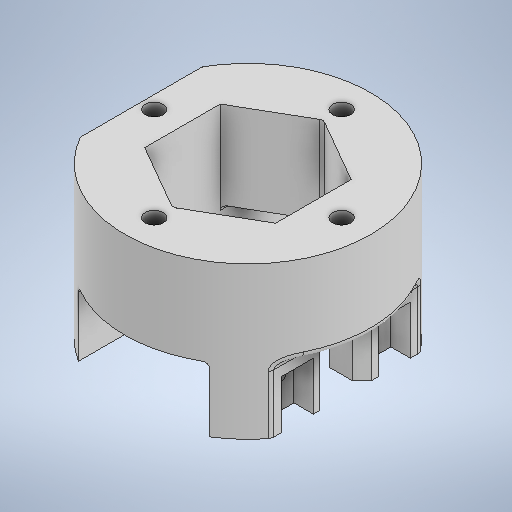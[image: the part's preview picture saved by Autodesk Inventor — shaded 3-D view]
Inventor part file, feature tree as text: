
AUTODESK INVENTOR PART (.ipt)
format: ipt  version: 2025 (Build 290162000, 162)  size: 421,888 bytes
history: native  units: mm
features: sketch x8, extrude x6, hole x2, pattern_circular x2, mirror x2, chamfer x1, fillet x1
ambient origin geometry x8: Origin, YZ Plane, XZ Plane, XY Plane, X Axis, Y Axis, Z Axis, Center Point
bodies: Solid1 (feature_tree)
feature tree (22):
  extrude  "Key Shape"  Depth=36.0mm
  extrude  "Side Walls"  Depth=27.0mm TaperAngle=0.0deg
  hole  "M5 Holes"  [1 undecoded]
  pattern_circular  "Circular Pattern1"  Count=2  [1 undecoded]
  extrude  "M4 Bolt Seats"  Depth=2.0mm
  hole  "M4 Holes"  [1 undecoded]
  mirror  "Mirror1"
  mirror  "Mirror2"
  chamfer  "Chamfer1"  Distance=6.0mm
  extrude  "Nut Seats"  Depth=2.0mm
  pattern_circular  "Circular Pattern2"  [2 undecoded]
  extrude  "Hollow Center"  Depth=10.0mm
  extrude  "Extrusion6"  Depth=2.0mm TaperAngle=45.0deg
  fillet  "Fillet10"  Radius=8.25mm
  sketch  "Sketch1"  dims[d0=82.0mm d1=36.0mm]
  sketch  "Sketch2"  dims[d2=3.0mm d3=27.0mm d4=0.0mm]
  sketch  "Sketch3"  dims[d5=20.25mm d6=10.0mm d7=20.0mm d8=0.0mm]
  sketch  "Sketch4"  dims[d9=5.6mm d10=6.0mm d11=4.0mm d12=2.0mm d13=90.0deg d14=8.0mm d15=20.594885mm d16=29.0mm]
  sketch  "Sketch5"  dims[d17=40.0mm d18=360.0deg d20=10.0mm]
  sketch  "Sketch6"  dims[d21=15.0mm]
  sketch  "Sketch7"  dims[d22=15.0mm d23=6.0mm d24=0.0mm]
  sketch  "Sketch8"  dims[d25=5.5mm d26=6.0mm d27=4.0mm d28=2.0mm d29=90.0deg d30=8.0mm d31=20.594885mm d32=15.0mm d33=10.0mm d40=10.0mm d42=3.0mm d43=2.0mm d44=45.0deg d46=8.25mm d47=4.0mm d48=0.0mm d49=40.0mm d50=360.0deg d52=40.5mm d53=27.0mm d54=0.0mm d55=1.5mm d56=4.0mm d57=0.0mm d58=2.0mm]
note: 5 required parameter values undecoded (feature->parameter linkage not recoverable at this tier; creation-order binding heuristic only, values carry confidence <= 0.55)
